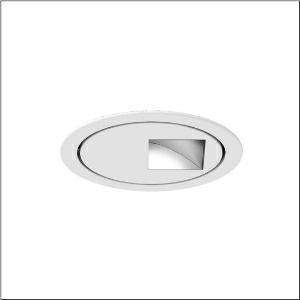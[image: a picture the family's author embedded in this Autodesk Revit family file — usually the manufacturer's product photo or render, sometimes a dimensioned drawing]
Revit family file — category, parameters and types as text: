
# Revit family: lunis_11_mini_round_51dk11b72wg21
name_source: partatom
category: Lighting Fixtures
units: mm (PartAtom-declared; Revit-internal decimal feet)

## family parameters
Cut with Voids When Loaded = No
Host = Face
Light Source = No
Part Type = Normal
Room Calculation Point = No
Round Connector Dimension = Use Diameter
Shared = No

## types (1)
- Lunis 11 mini round (1 x LED 4000K / CRI = 80 (unbekannt), 2470 lm, 4000K)
    Apparent Load = 28 VA
    CIE Flux Codes = 44 77 97 100 100
    Color Rendering = 80
    Color Temperature = 4000K
    Default Elevation = 1800 mm
    Description = Lunis 11 mini round, downlight, light control with wallwasher, of highly reflective aluminium, highly specular, light emission: direct distribution, LED rated luminous flux: 2.470lm, light colour: 840, control gear: ECG, with terminal, 3-pole, mains connection: 220..230V, AC/DC, 0/50..60Hz, LED module, luminaire module, of aluminium, highly specular, white, diameter: 176mm, clamping range: 1..40mm, recessing ring, of plastic, traffic white (RAL 9016), protection rating (complete): IP20, insulation class (complete): insulation class II (safety insulation), certification: CE, permissible ambient temperature for indoor applications: 0..+35°C, packaging unit: 1 piece
    Height = 0 mm  [stored 0 ft]
    Lamp = 1 x LED 4000K / CRI >= 80 (unbekannt)
    Lamp Light Flux = 2470 lm
    Lamp count = 1
    Length = 176 mm
    Luminous efficacy = 88 lm/W
    Manufacturer = Siteco
    ModVariant = No
    Model = 51DK11B72WG21
    Mounting Place = Ceiling
    Mounting Type = Recessed
    Number of Poles = 1
    OnlyDefault = Yes
    Power Factor = 1
    Product Name = Lunis 11 mini round
    Product group = downlight
    ProductGroupID = 400
    Protection Class = Protection class II
    Protection Degree = IP 20
    RLX_Detail_Level = 1
    RLX_Emergency_Light_Flux = 0 lm
    RLX_Emergency_Type = 0
    RLX_Emergency_Type_DB = No
    RlxData = <blob elided: 59249 chars, md5=bfd655c8>
    Socket = socket
    Standby Power = 0 W
    System Light Flux = 2470 lm
    System Power = 28 W
    Type Comments = Product without accessories
    Type Image = l_1004772.jpg
    URL = http://relux.com
    VarID = ---
    Voltage = 0 V
    Weight = 0.00 kg
    Width = 176 mm

note: [stored X ft] marks values corroborated as IEEE doubles in the binary element streams (Revit-internal decimal feet)

## geometry (parser evidence)
native form markers: Blend x4, Sweep x8
no freeform markers — native parametric forms only
